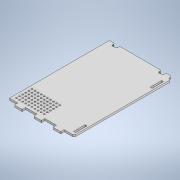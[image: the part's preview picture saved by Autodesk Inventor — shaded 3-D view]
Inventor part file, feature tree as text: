
AUTODESK INVENTOR PART (.ipt)
format: ipt  version: 2020 (Build 240168000, 168)  size: 302,080 bytes
history: native  units: mm
features: extrude x1, sketch x1
ambient origin geometry x8: Origin, YZ Plane, XZ Plane, XY Plane, X Axis, Y Axis, Z Axis, Center Point
bodies: Solid1 (feature_tree)
feature tree (2):
  extrude  "Extrusion1"  Depth=20.0mm
  sketch  "Sketch1"  dims[d2=21.75mm d3=20.0mm d4=30.0mm d5=20.0mm d6=30.0mm d7=20.0mm d8=9.0mm d9=1.0mm d14=108.0mm d15=14.0mm d19=9.0mm d24=12.7mm d25=167.25mm d26=3.0mm d27=3.0mm d28=3.0mm d29=12.7mm d30=6.0mm d31=3.0mm d32=5.0mm d33=4.25mm d34=5.25mm d35=30.0mm d37=8.0mm d38=4.0mm d39=100.0mm d41=8.0mm d42=60.0mm d44=8.0mm d47=9.0mm d48=9.0mm d49=5.0mm d50=0.0mm d52=250.0mm d53=22.5mm d51=0.5mm]
